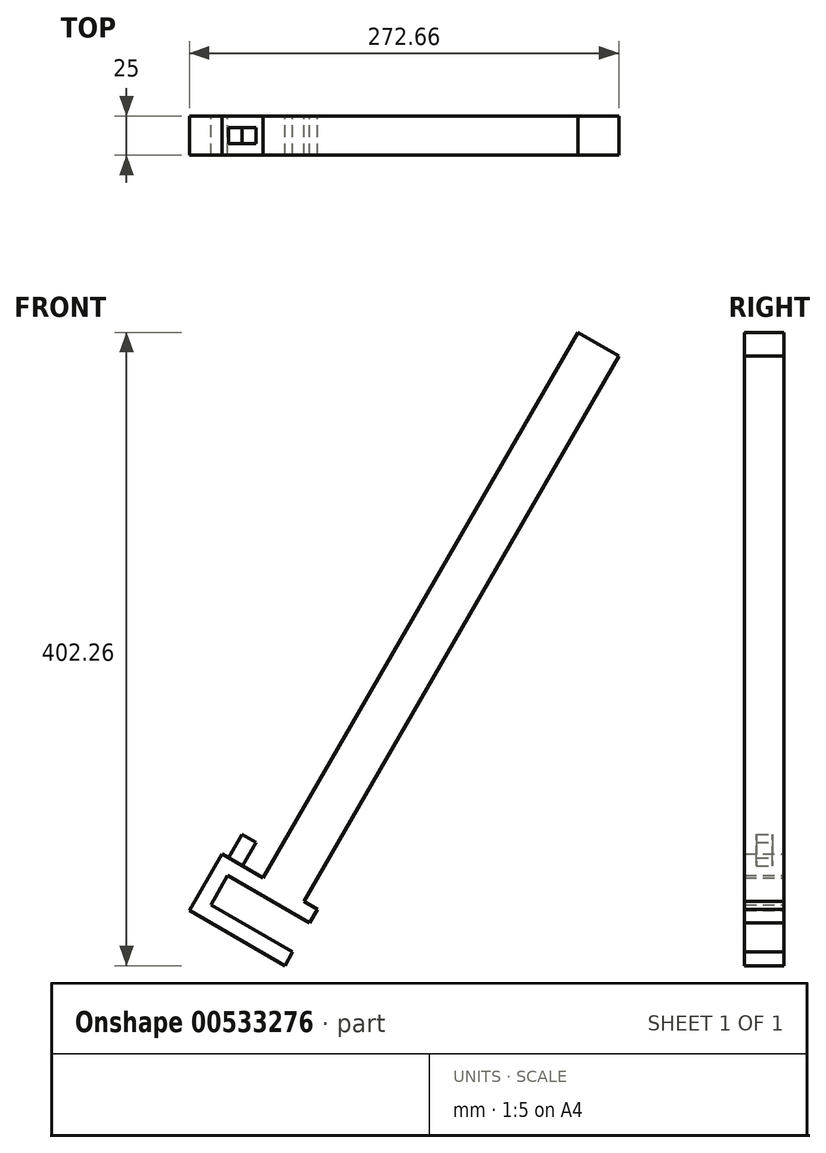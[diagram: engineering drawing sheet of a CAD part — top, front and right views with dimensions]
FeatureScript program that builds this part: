
annotation { "Feature Type Name" : "Feature", "Feature Type Description" : "" }
export const myFeature = defineFeature(function(context is Context, id is Id, definition is map)
    precondition{}
    {
        {
            var Q0;
            Q0=qCreatedBy(makeId("Front.planeOp"),FACE);
            var sketch = newSketch(context, id + "F0", { "sketchPlane" : qUnion([Q0])});
            skLineSegment(sketch, "E0.bottom", {"start": v(59.66, 10) * mm, "end": v(-0.34, 10) * mm});
            skLineSegment(sketch, "E0.left", {"start": v(59.66, 10) * mm, "end": v(59.66, 0) * mm});
            skLineSegment(sketch, "E1.bottom", {"start": v(59.66, 31.4) * mm, "end": v(-0.34, 31.4) * mm});
            skLineSegment(sketch, "E1.left", {"start": v(59.66, 31.4) * mm, "end": v(59.66, 41.4) * mm});
            skLineSegment(sketch, "E2.left", {"start": v(-0.34, 10) * mm, "end": v(-0.34, 31.4) * mm});
            skLineSegment(sketch, "E2.right", {"start": v(-10.34, 0) * mm, "end": v(-10.34, 41.4) * mm});
            skPoint(sketch, "E3.orphan", {"position": v(-0.34, 0) * mm});
            skLineSegment(sketch, "E4", {"start": v(59.66, 0) * mm, "end": v(-10.34, 0) * mm});
            skPoint(sketch, "E1.right.end.orphan", {"position": v(0, 41.4) * mm});
            skLineSegment(sketch, "E5", {"start": v(59.66, 41.4) * mm, "end": v(-10.34, 41.4) * mm});
            skSolve(sketch);
        }
        {
            var Q0;
            Q0 = qSketchRegion(id + "F0", true);
            extrude(context, id + "F1", {"entities" : qUnion([Q0]), "depth" : 25 * mm, "offsetDistance" : 25 * mm});
        }
        {
            var Q0;
            Q0=makeQuery(id+"F1.opExtrude","SWEPT_BODY",BODY,{"disambiguationData":[OSD([sQuery(id+"F0.wireOp",EDGE,"E0.bottom"),sQuery(id+"F0.wireOp",EDGE,"E0.left"),sQuery(id+"F0.wireOp",EDGE,"E1.bottom"),sQuery(id+"F0.wireOp",EDGE,"E1.left"),sQuery(id+"F0.wireOp",EDGE,"E2.left"),sQuery(id+"F0.wireOp",EDGE,"E2.right"),sQuery(id+"F0.wireOp",EDGE,"E4"),sQuery(id+"F0.wireOp",EDGE,"E5")])]});
            var Q1;
            Q1=makeQuery(id+"F1.opExtrude","SWEPT_EDGE",EDGE,{"disambiguationData":[OSD([sQuery(id+"F0.wireOp",EDGE,"E2.right"),sQuery(id+"F0.wireOp",EDGE,"E4")])]});
            transform(context, id + "F2", {"entities" : qUnion([Q0]), "transformType" : TransformType.ROTATION, "transformAxis" : qUnion([Q1]), "angle" : 30 * degree, "makeCopy" : false});
        }
        {
            var Q0;
            Q0=qCreatedBy(makeId("Front.planeOp"),FACE);
            var sketch = newSketch(context, id + "F3", { "sketchPlane" : qUnion([Q0])});
            skLineSegment(sketch, "E6", {"start": v(62.32, 5.85) * mm, "end": v(262.32, 352.26) * mm});
            skLineSegment(sketch, "E7", {"start": v(262.32, 352.26) * mm, "end": v(236.34, 367.26) * mm});
            skLineSegment(sketch, "E8", {"start": v(236.34, 367.26) * mm, "end": v(36.34, 20.85) * mm});
            skLineSegment(sketch, "E9", {"start": v(36.34, 20.85) * mm, "end": v(62.32, 5.85) * mm});
            skSolve(sketch);
        }
        {
            var Q0;
            Q0=makeQuery(id+"F3.imprint","IMPRINT",FACE,{"disambiguationData":[TD([[makeQuery(id+"F3.imprint","IMPRINT",EDGE,{"derivedFrom":sQuery(id+"F3.wireOp",EDGE,"E6")}),1.0]])]});
            extrude(context, id + "F4", {"entities" : qUnion([Q0]), "operationType" : NewBodyOperationType.ADD, "depth" : 25 * mm, "offsetDistance" : 25 * mm});
        }
        {
            var Q0;
            Q0=qCreatedBy(makeId("Front.planeOp"),FACE);
            var sketch = newSketch(context, id + "F5", { "sketchPlane" : qUnion([Q0])});
            skLineSegment(sketch, "E10", {"start": v(31.93, 43.12) * mm, "end": v(23.39, 28.33) * mm});
            skLineSegment(sketch, "E11", {"start": v(23.39, 28.33) * mm, "end": v(14.49, 33.47) * mm});
            skLineSegment(sketch, "E12", {"start": v(14.49, 33.47) * mm, "end": v(23.03, 48.26) * mm});
            skLineSegment(sketch, "E13", {"start": v(23.03, 48.26) * mm, "end": v(31.93, 43.12) * mm});
            skSolve(sketch);
        }
        {
            var Q0;
            Q0 = qSketchRegion(id + "F5", true);
            extrude(context, id + "F6", {"entities" : qUnion([Q0]), "operationType" : NewBodyOperationType.ADD, "depth" : 17.5 * mm, "offsetDistance" : 25 * mm, "hasSecondDirection" : true, "secondDirectionOppositeDirection" : false, "secondDirectionDepth" : 7.5 * mm});
        }
    });
